# Revit family: Drinking_Fountain-Haws_Corporation-Wall_Mounted_1107L
name_source: partatom
category: Plumbing Fixtures
units: mm (PartAtom-declared; Revit-internal decimal feet)

## family parameters
Always vertical = Yes
Cut with Voids When Loaded = No
Host = Wall
OmniClass Number = 23.65.70.14.11
OmniClass Title = Drinking Fountains/Coolers
Part Type = Normal
Room Calculation Point = No
Round Connector Dimension = Use Radius
Shared = Yes

## types (1)
- Not a Type - Load Type Catalog!
    Apparent Load = 0 VA
    Assembly Code = D2010810
    BIMobject category = Taps & Mixers
    BIMobject category code = sanitary-taps-mixers
    BIMobject main category = Sanitary
    BIMobject main category code = sanitary
    BP15 Panel = Yes
    BP7 Panel = Yes
    Back Panel = Metal - Haws Corporation - Polished Chrome - 5703M
    Basin Height = 4 1/4"
    Basin Width = 12"
    Bottle Filler 1920 = Yes
    Bowl = Metal - Haws Corporation - Polished Chrome - 5703M
    Brand url = https://www.hawsco.com
    CW Connection = Yes
    CWFU = 1
    Cost = $0
    Cost Note = For Cost information please visit the Resource tab in the Product Page URL
    Current = 0 A
    Date of publishing = 3/24/2014
    Design country = United States
    EAN code = https://611970315904
    Edition number = 1
    Electrical Connection Note = Electrical connection is only required for products that contain touchless sensors
    Flow = 0.00 GPM
    HW Connection = No
    HWFU = 0
    Keynote = 15410.A1
    Manufacturer = Haws Corporation 1455 Kleppe Lane Sparks, NV 89431
    Manufacturer country = United States
    Manufacturer name = Haws Corporation
    Masterformat 2014 Code = 22 47 13
    Masterformat 2014 Description = Drinking Fountains
    Material main = Metal
    Nominal height = 7"
    Nominal width = 12"
    Nr = 3
    Number of Poles = 1
    OmniClass Code = 23-31 31 00
    OmniClass Description = Drinking Fountains
    Power Factor = 1
    Product SKU = haws-1107l
    Product certification = http://www.csagroup.org
    Product family = Drinking Fountains/Coolers
    Product group = Wall Mounted Drinking Fountains
    QR code = http://bimobject.com
    Sanitary Radius = 5/8"
    Series = The Haws 1107 low profile barrier free drinking fountain with antimicrobial protection
    Supply No = 3
    Supply Radius = 1/4"
    Touchless Sensor = Yes
    Trim = Metal - Haws Corporation - Polished Chrome - 5703M
    Trim Plate = No
    Type Comments = Designed without a back panel
    URL = http://www.hawsco.com
    Uniclass 2015 Code = Pr_40_20_87_24
    Uniclass 2015 Name = Drinking fountains
    Vent Connection = No
    Voltage = 0 V
    WFU = 1
    Waste Connection = Yes
    Weight Net (Kg) = 26

## geometry (parser evidence)
native form markers: Sweep x10
no freeform markers — native parametric forms only
